# Revit family: Casement_30.5_G_Top_Hung_Standard
name_source: partatom
category: Windows
revit_build: Autodesk Revit 2014 (Build: 20130308_1515(x64)
units: mm (PartAtom-declared; Revit-internal decimal feet)

## types (12) — shared parameters
Aluminium Thickness = 1 mm  [stored 0.00328084 ft]
Bead SG Gap = 13 mm  [stored 0.0426509 ft]
Bottom Hung = No
Casement Dimension = 31 mm  [stored 0.101706 ft]
Custom Sash Height Bottom = 569 mm  [stored 1.8668 ft]
Custom Sash Height Top = 569 mm  [stored 1.8668 ft]
Custom Window Height = 1190 mm
DG Extrusion Start = 5 mm  [stored 0.0164042 ft]
DG Gasket Finish = Double Glazing Gasket Material
DG Thickness = 3 mm  [stored 0.00984252 ft]
Default Sill Height = 800 mm  [stored 2.62467 ft]
Depth Bead = 17 mm  [stored 0.0557743 ft]
Description = Window 30.5mm, Type G top hung
Double Glazing = No
Frame Center Offset = 15 mm  [stored 0.0492126 ft]
Height = 1200 mm
Height Panel 1 = 555 mm  [stored 1.82087 ft]
Height Panel 2 = 555 mm  [stored 1.82087 ft]
Height Panel 4 = 1140 mm  [stored 3.74016 ft]
Height Sash 1 = 539 mm
Height Sash 2 = 539 mm
Height Sash Bottom Opening = 569 mm  [stored 1.8668 ft]
Height Sash Top Opening = 569 mm  [stored 1.8668 ft]
Length Mullion = 1200 mm
Limit Fixed Pane Height Max = 1800 mm
Limit Fixed Pane Height Min = 200 mm  [stored 0.656168 ft]
Limit Fixed Pane Width Max = 1500 mm
Limit Fixed Pane Width Min = 200 mm  [stored 0.656168 ft]
Limit Sash Bottom Height Max Based On Top Sash = 1229 mm
Limit Sash Height Bottom Max = 750 mm  [stored 2.46063 ft]
Limit Sash Height Bottom Min = 300 mm  [stored 0.984252 ft]
Limit Sash Height Top Max = 750 mm  [stored 2.46063 ft]
Limit Sash Height Top Min = 300 mm  [stored 0.984252 ft]
Limit Sash Width Max = 1000 mm  [stored 3.28084 ft]
Limit Sash Width Min = 300 mm  [stored 0.984252 ft]
Limit Window Height Max = 1860 mm
Manufacturer = Crealco
Max System DG One Piece Thickness = 3 mm  [stored 0.00984252 ft]
Max System DG Unit Thickness = 18 mm  [stored 0.0590551 ft]
Model = Casement 30.5
Offset Bead SG Center Reversed = 15 mm  [stored 0.0492126 ft]
Offset Sash 1 Top = 23 mm  [stored 0.0754593 ft]
Offset Sash 2 Top = 608 mm  [stored 1.99475 ft]
Offset Sash Left = 23 mm  [stored 0.0754593 ft]
Offset Transom 1 Top = 585 mm  [stored 1.91929 ft]
Offset Window Exterior = 15 mm  [stored 0.0492126 ft]
Rough Width = 16 mm  [stored 0.0524934 ft]
SG Gasket Thickness = 6 mm  [stored 0.019685 ft]
Sash Center Offset = 12 mm  [stored 0.0393701 ft]
Sash Overlap = 7 mm  [stored 0.0229659 ft]
Sash Spacing Inner = 8 mm  [stored 0.0262467 ft]
Top Hung = Yes
URL = http://www.crealco.co.za
Wall Closure = By host
Width Bead = 15 mm  [stored 0.0492126 ft]
Width Profile = 30 mm  [stored 0.0984252 ft]
zero-valued in all types: Window Exterior Offset

## per-type parameters (varying)
- 305-1212DT-1000Pa: Area Pane Left Bottom=0.25 m²; Area Pane Left Top=0.25 m²; Area Pane Right=0.6 m²; Clearvue SHGC Value=0.803; Clearvue U Value=8.28; Custom Sash Width=569 mm  [stored 1.8668 ft]; Custom Windload=1000 mm  [stored 3.28084 ft]; Custom Window Width=1190 mm; DG Thickness Calc=3 mm  [stored 0.00984252 ft]; Depth Mullion=32 mm; Energy Advantage SHGC Value=0.719; Energy Advantage U Value=6.28; Intruderprufe LowE SHGC Value=0.677; Intruderprufe LowE U Value=6.14; Intruderprufe SHGC Value=0.765; Intruderprufe U Value=8.09; Length Transom=555 mm  [stored 1.82087 ft]; Limit Window Width Max=2145 mm; Limit Window Width Min=845 mm  [stored 2.77231 ft]; Max Pane Area=0.6 m²; Mullion Depth Windload Based=32 mm; Offset Mullion Left=585 mm  [stored 1.91929 ft]; Offset Panel 4 Left=615 mm  [stored 2.01772 ft]; Width=1190 mm; Width Panel 1=555 mm  [stored 1.82087 ft]; Width Panel 2=555 mm  [stored 1.82087 ft]; Width Panel 4=545 mm; Width Sash 1=539 mm; Width Sash 2=539 mm; Width Sash Opening=569 mm  [stored 1.8668 ft]; Windload Design=1000 mm  [stored 3.28084 ft]
- 305-1212DT-1500Pa: Area Pane Left Bottom=0.25 m²; Area Pane Left Top=0.25 m²; Area Pane Right=0.6 m²; Clearvue SHGC Value=0.804; Clearvue U Value=8.28; Custom Sash Width=569 mm  [stored 1.8668 ft]; Custom Windload=1500 mm; Custom Window Width=1190 mm; DG Thickness Calc=3 mm  [stored 0.00984252 ft]; Depth Mullion=54 mm  [stored 0.177165 ft]; Energy Advantage SHGC Value=0.721; Energy Advantage U Value=6.38; Intruderprufe LowE SHGC Value=0.679; Intruderprufe LowE U Value=6.24; Intruderprufe SHGC Value=0.764; Intruderprufe U Value=8.09; Length Transom=555 mm  [stored 1.82087 ft]; Limit Window Width Max=2145 mm; Limit Window Width Min=845 mm  [stored 2.77231 ft]; Max Pane Area=0.6 m²; Mullion Depth Windload Based=54 mm  [stored 0.177165 ft]; Offset Mullion Left=585 mm  [stored 1.91929 ft]; Offset Panel 4 Left=615 mm  [stored 2.01772 ft]; Width=1190 mm; Width Panel 1=555 mm  [stored 1.82087 ft]; Width Panel 2=555 mm  [stored 1.82087 ft]; Width Panel 4=545 mm; Width Sash 1=539 mm; Width Sash 2=539 mm; Width Sash Opening=569 mm  [stored 1.8668 ft]; Windload Design=1500 mm
- 305-1512DT-1000Pa: Area Pane Left Bottom=0.25 m²; Area Pane Left Top=0.25 m²; Area Pane Right=0.94 m²; Clearvue SHGC Value=0.803; Clearvue U Value=8.81; Custom Sash Width=569 mm  [stored 1.8668 ft]; Custom Windload=1000 mm  [stored 3.28084 ft]; Custom Window Width=1490 mm; DG Thickness Calc=3 mm  [stored 0.00984252 ft]; Depth Mullion=54 mm  [stored 0.177165 ft]; Energy Advantage SHGC Value=0.819; Energy Advantage U Value=6.61; Intruderprufe LowE SHGC Value=0.77; Intruderprufe LowE U Value=6.46; Intruderprufe SHGC Value=0.869; Intruderprufe U Value=8.61; Length Transom=555 mm  [stored 1.82087 ft]; Limit Window Width Max=2145 mm; Limit Window Width Min=845 mm  [stored 2.77231 ft]; Max Pane Area=0.94 m²; Mullion Depth Windload Based=54 mm  [stored 0.177165 ft]; Offset Mullion Left=585 mm  [stored 1.91929 ft]; Offset Panel 4 Left=615 mm  [stored 2.01772 ft]; Width=1490 mm; Width Panel 1=555 mm  [stored 1.82087 ft]; Width Panel 2=555 mm  [stored 1.82087 ft]; Width Panel 4=845 mm  [stored 2.77231 ft]; Width Sash 1=539 mm; Width Sash 2=539 mm; Width Sash Opening=569 mm  [stored 1.8668 ft]; Windload Design=1000 mm  [stored 3.28084 ft]
- 305-1812DT-1000Pa: Area Pane Left Bottom=0.39 m²; Area Pane Left Top=0.39 m²; Area Pane Right=0.96 m²; Clearvue SHGC Value=0.861; Clearvue U Value=8.19; Custom Sash Width=854 mm  [stored 2.80184 ft]; Custom Windload=1000 mm  [stored 3.28084 ft]; Custom Window Width=1790 mm; DG Thickness Calc=3 mm  [stored 0.00984252 ft]; Depth Mullion=54 mm  [stored 0.177165 ft]; Energy Advantage SHGC Value=0.771; Energy Advantage U Value=6.11; Intruderprufe LowE SHGC Value=0.542; Intruderprufe LowE U Value=5.98; Intruderprufe SHGC Value=0.818; Intruderprufe U Value=8; Length Transom=840 mm  [stored 2.75591 ft]; Limit Window Width Max=2430 mm; Limit Window Width Min=1130 mm  [stored 3.70735 ft]; Max Pane Area=0.96 m²; Mullion Depth Windload Based=54 mm  [stored 0.177165 ft]; Offset Mullion Left=870 mm  [stored 2.85433 ft]; Offset Panel 4 Left=900 mm  [stored 2.95276 ft]; Width=1790 mm; Width Panel 1=840 mm  [stored 2.75591 ft]; Width Panel 2=840 mm  [stored 2.75591 ft]; Width Panel 4=860 mm; Width Sash 1=824 mm; Width Sash 2=824 mm; Width Sash Opening=854 mm  [stored 2.80184 ft]; Windload Design=1000 mm  [stored 3.28084 ft]
- 305-2412DT-1000Pa: Area Pane Left Bottom=0.39 m²; Area Pane Left Top=0.39 m²; Area Pane Right=1.64 m²; Clearvue SHGC Value=0; Clearvue U Value=7.9; Custom Sash Width=854 mm  [stored 2.80184 ft]; Custom Windload=1000 mm  [stored 3.28084 ft]; Custom Window Width=2390 mm; DG Thickness Calc=4 mm  [stored 0.0131234 ft]; Depth Mullion=54 mm  [stored 0.177165 ft]; Energy Advantage SHGC Value=0; Energy Advantage U Value=7.9; Intruderprufe LowE SHGC Value=0.571; Intruderprufe LowE U Value=4.32; Intruderprufe SHGC Value=0.647; Intruderprufe U Value=5.94; Length Transom=840 mm  [stored 2.75591 ft]; Limit Window Width Max=2430 mm; Limit Window Width Min=1130 mm  [stored 3.70735 ft]; Max Pane Area=1.64 m²; Mullion Depth Windload Based=54 mm  [stored 0.177165 ft]; Offset Mullion Left=870 mm  [stored 2.85433 ft]; Offset Panel 4 Left=900 mm  [stored 2.95276 ft]; Width=2390 mm; Width Panel 1=840 mm  [stored 2.75591 ft]; Width Panel 2=840 mm  [stored 2.75591 ft]; Width Panel 4=1460 mm; Width Sash 1=824 mm; Width Sash 2=824 mm; Width Sash Opening=854 mm  [stored 2.80184 ft]; Windload Design=1000 mm  [stored 3.28084 ft]
- 305-1212DT-2000Pa: Area Pane Left Bottom=0.25 m²; Area Pane Left Top=0.25 m²; Area Pane Right=0.6 m²; Clearvue SHGC Value=0.804; Clearvue U Value=8.28; Custom Sash Width=569 mm  [stored 1.8668 ft]; Custom Windload=2000 mm; Custom Window Width=1190 mm; DG Thickness Calc=3 mm  [stored 0.00984252 ft]; Depth Mullion=54 mm  [stored 0.177165 ft]; Energy Advantage SHGC Value=0.721; Energy Advantage U Value=6.38; Intruderprufe LowE SHGC Value=0.679; Intruderprufe LowE U Value=6.24; Intruderprufe SHGC Value=0.764; Intruderprufe U Value=8.09; Length Transom=555 mm  [stored 1.82087 ft]; Limit Window Width Max=2145 mm; Limit Window Width Min=845 mm  [stored 2.77231 ft]; Max Pane Area=0.6 m²; Mullion Depth Windload Based=54 mm  [stored 0.177165 ft]; Offset Mullion Left=585 mm  [stored 1.91929 ft]; Offset Panel 4 Left=615 mm  [stored 2.01772 ft]; Width=1190 mm; Width Panel 1=555 mm  [stored 1.82087 ft]; Width Panel 2=555 mm  [stored 1.82087 ft]; Width Panel 4=545 mm; Width Sash 1=539 mm; Width Sash 2=539 mm; Width Sash Opening=569 mm  [stored 1.8668 ft]; Windload Design=2000 mm
- 305-1512DT-1500Pa: Area Pane Left Bottom=0.25 m²; Area Pane Left Top=0.25 m²; Area Pane Right=0.94 m²; Clearvue SHGC Value=0.803; Clearvue U Value=8.81; Custom Sash Width=569 mm  [stored 1.8668 ft]; Custom Windload=1500 mm; Custom Window Width=1490 mm; DG Thickness Calc=3 mm  [stored 0.00984252 ft]; Depth Mullion=54 mm  [stored 0.177165 ft]; Energy Advantage SHGC Value=0.819; Energy Advantage U Value=6.61; Intruderprufe LowE SHGC Value=0.77; Intruderprufe LowE U Value=6.46; Intruderprufe SHGC Value=0.869; Intruderprufe U Value=8.61; Length Transom=555 mm  [stored 1.82087 ft]; Limit Window Width Max=2145 mm; Limit Window Width Min=845 mm  [stored 2.77231 ft]; Max Pane Area=0.94 m²; Mullion Depth Windload Based=54 mm  [stored 0.177165 ft]; Offset Mullion Left=585 mm  [stored 1.91929 ft]; Offset Panel 4 Left=615 mm  [stored 2.01772 ft]; Width=1490 mm; Width Panel 1=555 mm  [stored 1.82087 ft]; Width Panel 2=555 mm  [stored 1.82087 ft]; Width Panel 4=845 mm  [stored 2.77231 ft]; Width Sash 1=539 mm; Width Sash 2=539 mm; Width Sash Opening=569 mm  [stored 1.8668 ft]; Windload Design=1500 mm
- 305-1512DT-2000Pa: Area Pane Left Bottom=0.25 m²; Area Pane Left Top=0.25 m²; Area Pane Right=0.94 m²; Clearvue SHGC Value=0.803; Clearvue U Value=8.81; Custom Sash Width=569 mm  [stored 1.8668 ft]; Custom Windload=2000 mm; Custom Window Width=1490 mm; DG Thickness Calc=3 mm  [stored 0.00984252 ft]; Depth Mullion=54 mm  [stored 0.177165 ft]; Energy Advantage SHGC Value=0.819; Energy Advantage U Value=6.61; Intruderprufe LowE SHGC Value=0.77; Intruderprufe LowE U Value=6.46; Intruderprufe SHGC Value=0.869; Intruderprufe U Value=8.61; Length Transom=555 mm  [stored 1.82087 ft]; Limit Window Width Max=2145 mm; Limit Window Width Min=845 mm  [stored 2.77231 ft]; Max Pane Area=0.94 m²; Mullion Depth Windload Based=54 mm  [stored 0.177165 ft]; Offset Mullion Left=585 mm  [stored 1.91929 ft]; Offset Panel 4 Left=615 mm  [stored 2.01772 ft]; Width=1490 mm; Width Panel 1=555 mm  [stored 1.82087 ft]; Width Panel 2=555 mm  [stored 1.82087 ft]; Width Panel 4=845 mm  [stored 2.77231 ft]; Width Sash 1=539 mm; Width Sash 2=539 mm; Width Sash Opening=569 mm  [stored 1.8668 ft]; Windload Design=2000 mm
- 305-1812DT-1500Pa: Area Pane Left Bottom=0.39 m²; Area Pane Left Top=0.39 m²; Area Pane Right=0.96 m²; Clearvue SHGC Value=0.861; Clearvue U Value=8.19; Custom Sash Width=854 mm  [stored 2.80184 ft]; Custom Windload=1500 mm; Custom Window Width=1790 mm; DG Thickness Calc=3 mm  [stored 0.00984252 ft]; Depth Mullion=54 mm  [stored 0.177165 ft]; Energy Advantage SHGC Value=0.771; Energy Advantage U Value=6.11; Intruderprufe LowE SHGC Value=0.542; Intruderprufe LowE U Value=5.98; Intruderprufe SHGC Value=0.818; Intruderprufe U Value=8; Length Transom=840 mm  [stored 2.75591 ft]; Limit Window Width Max=2430 mm; Limit Window Width Min=1130 mm  [stored 3.70735 ft]; Max Pane Area=0.96 m²; Mullion Depth Windload Based=54 mm  [stored 0.177165 ft]; Offset Mullion Left=870 mm  [stored 2.85433 ft]; Offset Panel 4 Left=900 mm  [stored 2.95276 ft]; Width=1790 mm; Width Panel 1=840 mm  [stored 2.75591 ft]; Width Panel 2=840 mm  [stored 2.75591 ft]; Width Panel 4=860 mm; Width Sash 1=824 mm; Width Sash 2=824 mm; Width Sash Opening=854 mm  [stored 2.80184 ft]; Windload Design=1500 mm
- 305-1812DT-2000Pa: Area Pane Left Bottom=0.39 m²; Area Pane Left Top=0.39 m²; Area Pane Right=0.96 m²; Clearvue SHGC Value=0.861; Clearvue U Value=8.19; Custom Sash Width=854 mm  [stored 2.80184 ft]; Custom Windload=2000 mm; Custom Window Width=1790 mm; DG Thickness Calc=3 mm  [stored 0.00984252 ft]; Depth Mullion=54 mm  [stored 0.177165 ft]; Energy Advantage SHGC Value=0.771; Energy Advantage U Value=6.11; Intruderprufe LowE SHGC Value=0.542; Intruderprufe LowE U Value=5.98; Intruderprufe SHGC Value=0.818; Intruderprufe U Value=8; Length Transom=840 mm  [stored 2.75591 ft]; Limit Window Width Max=2430 mm; Limit Window Width Min=1130 mm  [stored 3.70735 ft]; Max Pane Area=0.96 m²; Mullion Depth Windload Based=54 mm  [stored 0.177165 ft]; Offset Mullion Left=870 mm  [stored 2.85433 ft]; Offset Panel 4 Left=900 mm  [stored 2.95276 ft]; Width=1790 mm; Width Panel 1=840 mm  [stored 2.75591 ft]; Width Panel 2=840 mm  [stored 2.75591 ft]; Width Panel 4=860 mm; Width Sash 1=824 mm; Width Sash 2=824 mm; Width Sash Opening=854 mm  [stored 2.80184 ft]; Windload Design=2000 mm
- 305-2412DT-1500Pa: Area Pane Left Bottom=0.39 m²; Area Pane Left Top=0.39 m²; Area Pane Right=1.64 m²; Clearvue SHGC Value=0; Clearvue U Value=7.9; Custom Sash Width=854 mm  [stored 2.80184 ft]; Custom Windload=1500 mm; Custom Window Width=2390 mm; DG Thickness Calc=4 mm  [stored 0.0131234 ft]; Depth Mullion=54 mm  [stored 0.177165 ft]; Energy Advantage SHGC Value=0; Energy Advantage U Value=7.9; Intruderprufe LowE SHGC Value=0.571; Intruderprufe LowE U Value=4.32; Intruderprufe SHGC Value=0.647; Intruderprufe U Value=5.94; Length Transom=840 mm  [stored 2.75591 ft]; Limit Window Width Max=2430 mm; Limit Window Width Min=1130 mm  [stored 3.70735 ft]; Max Pane Area=1.64 m²; Mullion Depth Windload Based=54 mm  [stored 0.177165 ft]; Offset Mullion Left=870 mm  [stored 2.85433 ft]; Offset Panel 4 Left=900 mm  [stored 2.95276 ft]; Width=2390 mm; Width Panel 1=840 mm  [stored 2.75591 ft]; Width Panel 2=840 mm  [stored 2.75591 ft]; Width Panel 4=1460 mm; Width Sash 1=824 mm; Width Sash 2=824 mm; Width Sash Opening=854 mm  [stored 2.80184 ft]; Windload Design=1500 mm
- 305-2412DT-2000Pa: Area Pane Left Bottom=0.39 m²; Area Pane Left Top=0.39 m²; Area Pane Right=1.64 m²; Clearvue SHGC Value=0; Clearvue U Value=7.9; Custom Sash Width=854 mm  [stored 2.80184 ft]; Custom Windload=2000 mm; Custom Window Width=2390 mm; DG Thickness Calc=4 mm  [stored 0.0131234 ft]; Depth Mullion=54 mm  [stored 0.177165 ft]; Energy Advantage SHGC Value=0; Energy Advantage U Value=7.9; Intruderprufe LowE SHGC Value=0.571; Intruderprufe LowE U Value=4.32; Intruderprufe SHGC Value=0.647; Intruderprufe U Value=5.94; Length Transom=840 mm  [stored 2.75591 ft]; Limit Window Width Max=2430 mm; Limit Window Width Min=1130 mm  [stored 3.70735 ft]; Max Pane Area=1.64 m²; Mullion Depth Windload Based=54 mm  [stored 0.177165 ft]; Offset Mullion Left=870 mm  [stored 2.85433 ft]; Offset Panel 4 Left=900 mm  [stored 2.95276 ft]; Width=2390 mm; Width Panel 1=840 mm  [stored 2.75591 ft]; Width Panel 2=840 mm  [stored 2.75591 ft]; Width Panel 4=1460 mm; Width Sash 1=824 mm; Width Sash 2=824 mm; Width Sash Opening=854 mm  [stored 2.80184 ft]; Windload Design=2000 mm

note: [stored X ft] marks values corroborated as IEEE doubles in the binary element streams (Revit-internal decimal feet)

## geometry (parser evidence)
native form markers: Blend x4, Extrusion x1, Sweep x28
no freeform markers — native parametric forms only
